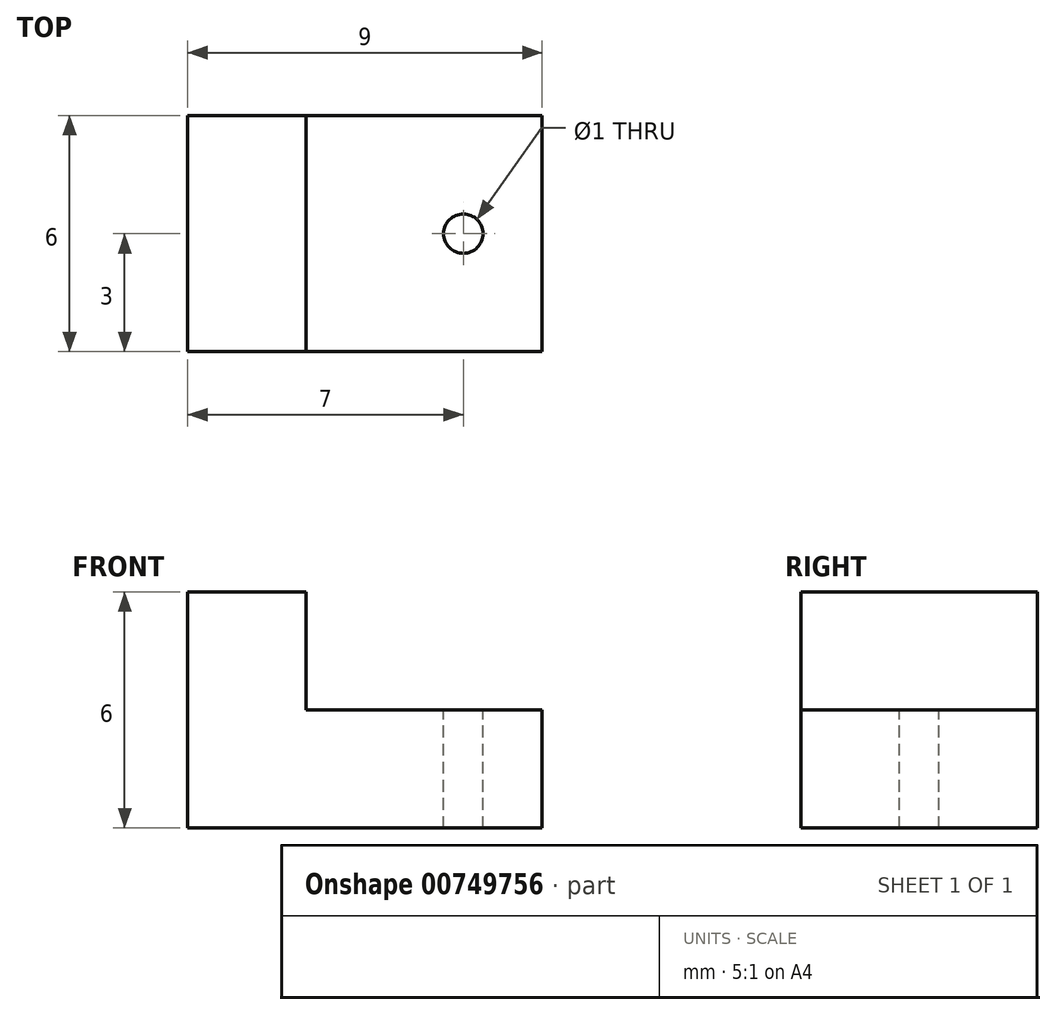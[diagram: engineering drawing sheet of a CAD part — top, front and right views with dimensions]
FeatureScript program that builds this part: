
annotation { "Feature Type Name" : "Feature", "Feature Type Description" : "" }
export const myFeature = defineFeature(function(context is Context, id is Id, definition is map)
    precondition{}
    {
        {
            var Q0;
            Q0=qCreatedBy(makeId("Top.planeOp"),FACE);
            var sketch = newSketch(context, id + "F0", { "sketchPlane" : qUnion([Q0])});
            skLineSegment(sketch, "E0", {"start": v(0, 0) * mm, "end": v(0, 6) * mm});
            skLineSegment(sketch, "E1", {"start": v(3, 6) * mm, "end": v(0, 6) * mm});
            skLineSegment(sketch, "E2", {"start": v(3, 6) * mm, "end": v(3, 0) * mm});
            skLineSegment(sketch, "E3", {"start": v(3, 0) * mm, "end": v(0, 0) * mm});
            skLineSegment(sketch, "E4", {"start": v(3, 0) * mm, "end": v(9, 0) * mm});
            skLineSegment(sketch, "E5", {"start": v(9, 6) * mm, "end": v(3, 6) * mm});
            skLineSegment(sketch, "E6", {"start": v(9, 6) * mm, "end": v(9, 0) * mm});
            skSolve(sketch);
        }
        {
            var Q0;
            Q0=makeQuery(id+"F0.imprint","IMPRINT",FACE,{"disambiguationData":[TD([[makeQuery(id+"F0.imprint","IMPRINT",EDGE,{"derivedFrom":sQuery(id+"F0.wireOp",EDGE,"E0")}),-1.0]])]});
            extrude(context, id + "F1", {"entities" : qUnion([Q0]), "depth" : 6 * mm, "offsetDistance" : 25 * mm});
        }
        {
            var Q0;
            Q0=makeQuery(id+"F0.imprint","IMPRINT",FACE,{"disambiguationData":[TD([[makeQuery(id+"F0.imprint","IMPRINT",EDGE,{"derivedFrom":sQuery(id+"F0.wireOp",EDGE,"E2")}),1.0]])]});
            extrude(context, id + "F2", {"entities" : qUnion([Q0]), "operationType" : NewBodyOperationType.ADD, "depth" : 3 * mm, "offsetDistance" : 25 * mm});
        }
        {
            var Q0;
            Q0=makeQuery(id+"F2.opExtrude","CAP_FACE",FACE,{"disambiguationData":[OSD([sQuery(id+"F0.wireOp",EDGE,"E2"),sQuery(id+"F0.wireOp",EDGE,"E4"),sQuery(id+"F0.wireOp",EDGE,"E5"),sQuery(id+"F0.wireOp",EDGE,"E6")])],"isStart":false});
            var sketch = newSketch(context, id + "F3", { "sketchPlane" : qUnion([Q0])});
            skLineSegment(sketch, "E7", {"start": v(9, 3) * mm, "end": v(7, 3) * mm});
            skCircle(sketch, "E8", {"center": v(7, 3) * mm, "radius": 0.5 * mm});
            skSolve(sketch);
        }
        {
            var Q0;
            Q0=makeQuery(id+"F3.imprint","IMPRINT",FACE,{"disambiguationData":[TD([[makeQuery(id+"F3.imprint","IMPRINT",EDGE,{"derivedFrom":sQuery(id+"F3.wireOp",EDGE,"E8")}),1.0]])]});
            extrude(context, id + "F4", {"entities" : qUnion([Q0]), "operationType" : NewBodyOperationType.REMOVE, "endBound" : BoundingType.THROUGH_ALL, "oppositeDirection" : true, "depth" : 25 * mm, "offsetDistance" : 25 * mm});
        }
    });
